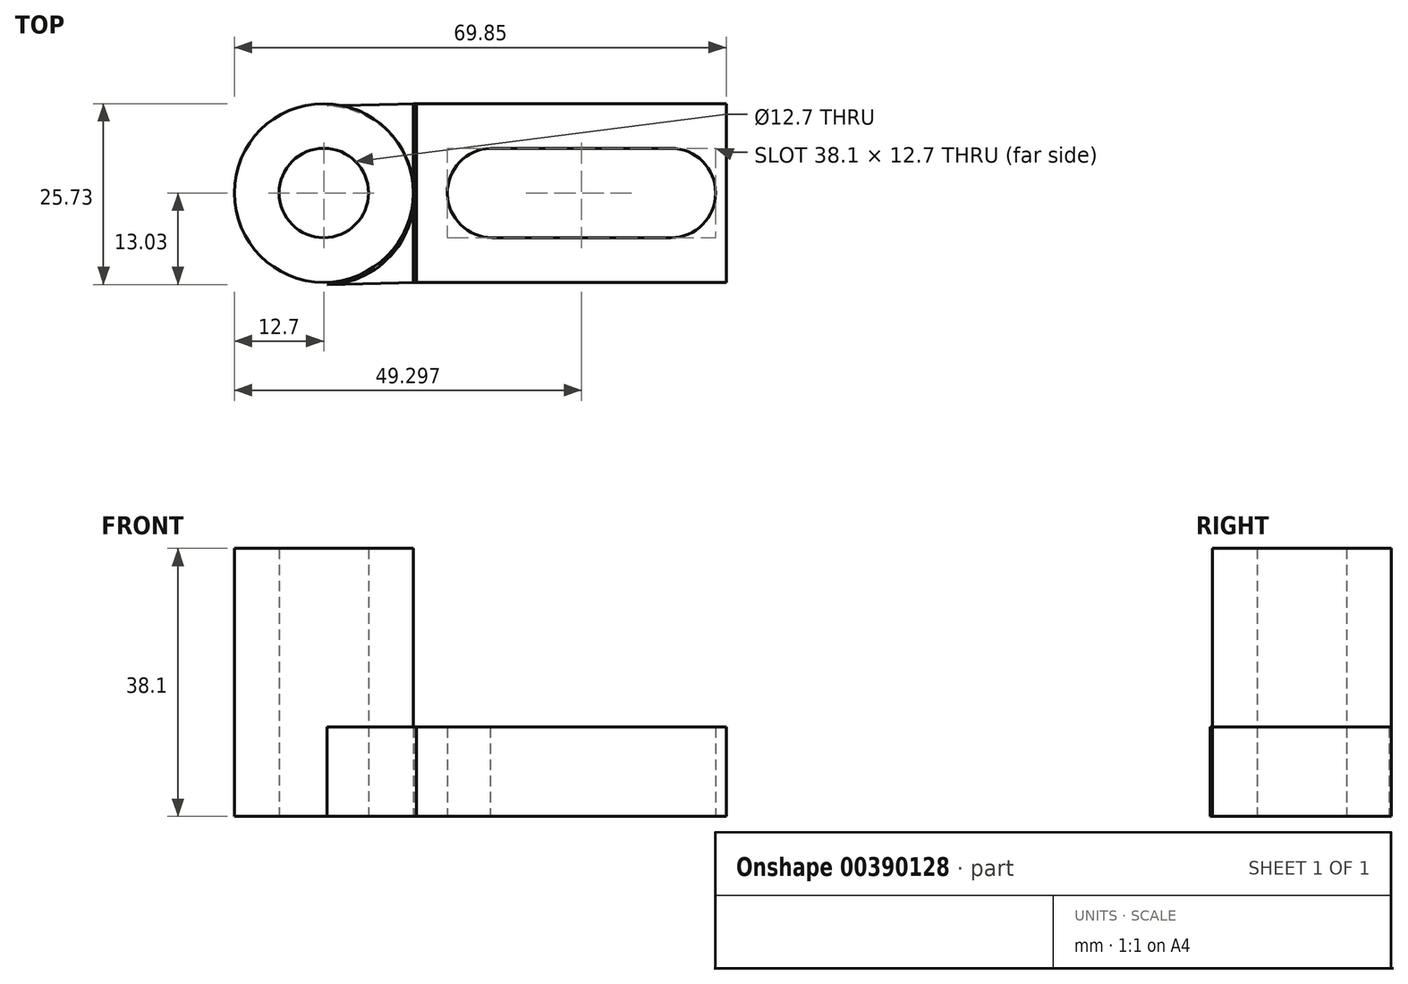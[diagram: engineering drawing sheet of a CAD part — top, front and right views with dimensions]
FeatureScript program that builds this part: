
annotation { "Feature Type Name" : "Feature", "Feature Type Description" : "" }
export const myFeature = defineFeature(function(context is Context, id is Id, definition is map)
    precondition{}
    {
        {
            var Q0;
            Q0=qCreatedBy(makeId("Front.planeOp"),FACE);
            var sketch = newSketch(context, id + "F0", { "sketchPlane" : qUnion([Q0])});
            skLineSegment(sketch, "E0", {"start": v(0, 0) * mm, "end": v(69.85, 0) * mm});
            skLineSegment(sketch, "E1", {"start": v(69.85, 0) * mm, "end": v(69.85, 12.7) * mm});
            skLineSegment(sketch, "E2", {"start": v(69.85, 12.7) * mm, "end": v(25.4, 12.7) * mm});
            skLineSegment(sketch, "E3", {"start": v(25.4, 12.7) * mm, "end": v(25.4, 38.1) * mm});
            skLineSegment(sketch, "E4", {"start": v(25.4, 38.1) * mm, "end": v(0, 38.1) * mm});
            skLineSegment(sketch, "E5", {"start": v(0, 38.1) * mm, "end": v(0, 0) * mm});
            skSolve(sketch);
        }
        {
            var Q0;
            Q0=makeQuery(id+"F0.imprint","IMPRINT",FACE,{"disambiguationData":[TD([[makeQuery(id+"F0.imprint","IMPRINT",EDGE,{"derivedFrom":sQuery(id+"F0.wireOp",EDGE,"E0")}),1.0]])]});
            extrude(context, id + "F1", {"entities" : qUnion([Q0]), "depth" : 25.4 * mm});
        }
        {
            var Q0;
            Q0=qCreatedBy(makeId("Top.planeOp"),FACE);
            var sketch = newSketch(context, id + "F2", { "sketchPlane" : qUnion([Q0])});
            skCircle(sketch, "E6", {"center": v(36.6, -12.7) * mm, "radius": 6.35 * mm});
            skCircle(sketch, "E7", {"center": v(62, -12.7) * mm, "radius": 6.35 * mm});
            skLineSegment(sketch, "E8", {"start": v(36.35, -6.35) * mm, "end": v(62, -6.35) * mm});
            skLineSegment(sketch, "E9", {"start": v(62, -6.35) * mm, "end": v(62, -19.05) * mm});
            skLineSegment(sketch, "E10", {"start": v(62, -19.05) * mm, "end": v(36.6, -19.05) * mm});
            skLineSegment(sketch, "E11", {"start": v(36.6, -19.05) * mm, "end": v(36.35, -6.35) * mm});
            skLineSegment(sketch, "E12", {"start": v(0, 0) * mm, "end": v(0, -25.4) * mm});
            skLineSegment(sketch, "E13", {"start": v(0, -25.4) * mm, "end": v(25.4, -25.4) * mm});
            skLineSegment(sketch, "E14", {"start": v(25.4, -25.4) * mm, "end": v(25.4, 0) * mm});
            skLineSegment(sketch, "E15", {"start": v(25.4, 0) * mm, "end": v(0, 0) * mm});
            skSolve(sketch);
        }
        {
            var Q0;
            {var subQ0=sQuery(id+"F2.wireOp",EDGE,"E10");Q0=makeQuery(id+"F2.imprint","IMPRINT",FACE,{"disambiguationData":[TD([[makeQuery(id+"F2.imprint","IMPRINT",EDGE,{"derivedFrom":subQ0}),-1.0]])]});}
            var Q1;
            {var subQ0=sQuery(id+"F2.wireOp",EDGE,"E9");Q1=makeQuery(id+"F2.imprint","IMPRINT",FACE,{"disambiguationData":[TD([[makeQuery(id+"F2.imprint","IMPRINT",EDGE,{"derivedFrom":subQ0}),-1.0]])]});}
            var Q2;
            {var subQ0=sQuery(id+"F2.wireOp",EDGE,"E9");Q2=makeQuery(id+"F2.imprint","IMPRINT",FACE,{"disambiguationData":[TD([[makeQuery(id+"F2.imprint","IMPRINT",EDGE,{"derivedFrom":subQ0}),1.0]])]});}
            var Q3;
            {var subQ0=sQuery(id+"F2.wireOp",EDGE,"E11");Q3=makeQuery(id+"F2.imprint","IMPRINT",FACE,{"disambiguationData":[TD([[makeQuery(id+"F2.imprint","IMPRINT",EDGE,{"derivedFrom":subQ0}),-1.0]])]});}
            var Q4;
            {var subQ0=sQuery(id+"F2.wireOp",EDGE,"E11");Q4=makeQuery(id+"F2.imprint","IMPRINT",FACE,{"disambiguationData":[TD([[makeQuery(id+"F2.imprint","IMPRINT",EDGE,{"derivedFrom":subQ0}),1.0]])]});}
            extrude(context, id + "F3", {"entities" : qUnion([Q0, Q1, Q2, Q3, Q4]), "operationType" : NewBodyOperationType.REMOVE, "depth" : 50.8 * mm});
        }
        {
            var Q0;
            Q0=qCreatedBy(makeId("Top.planeOp"),FACE);
            var sketch = newSketch(context, id + "F4", { "sketchPlane" : qUnion([Q0])});
            skCircle(sketch, "E16", {"center": v(12.7, -12.7) * mm, "radius": 6.35 * mm});
            skArc(sketch, "E17", {"start": v(12.7, -25.4) * mm, "mid": v(0, -12.7) * mm, "end": v(12.7, 0) * mm});
            skLineSegment(sketch, "E18", {"start": v(12.7, 0) * mm, "end": v(0, 0) * mm});
            skLineSegment(sketch, "E19", {"start": v(0, 0) * mm, "end": v(0, -25.4) * mm});
            skLineSegment(sketch, "E20", {"start": v(0, -25.4) * mm, "end": v(12.7, -25.4) * mm});
            skArc(sketch, "E21", {"start": v(12.7, 0) * mm, "mid": v(25.4, -12.7) * mm, "end": v(12.7, -25.4) * mm});
            skLineSegment(sketch, "E22", {"start": v(12.7, -25.4) * mm, "end": v(25.4, -25.4) * mm});
            skLineSegment(sketch, "E23", {"start": v(25.4, -25.4) * mm, "end": v(25.4, 0) * mm});
            skLineSegment(sketch, "E24", {"start": v(25.4, 0) * mm, "end": v(12.7, 0) * mm});
            skSolve(sketch);
        }
        {
            var Q0;
            {var subQ0=sQuery(id+"F4.wireOp",EDGE,"E20");Q0=makeQuery(id+"F4.imprint","IMPRINT",FACE,{"disambiguationData":[TD([[makeQuery(id+"F4.imprint","IMPRINT",EDGE,{"derivedFrom":subQ0}),1.0]])]});}
            var Q1;
            {var subQ0=sQuery(id+"F4.wireOp",EDGE,"E18");Q1=makeQuery(id+"F4.imprint","IMPRINT",FACE,{"disambiguationData":[TD([[makeQuery(id+"F4.imprint","IMPRINT",EDGE,{"derivedFrom":subQ0}),1.0]])]});}
            var Q2;
            {var subQ0=sQuery(id+"F4.wireOp",EDGE,"E24");Q2=makeQuery(id+"F4.imprint","IMPRINT",FACE,{"disambiguationData":[TD([[makeQuery(id+"F4.imprint","IMPRINT",EDGE,{"derivedFrom":subQ0}),1.0]])]});}
            var Q3;
            {var subQ0=sQuery(id+"F4.wireOp",EDGE,"E22");Q3=makeQuery(id+"F4.imprint","IMPRINT",FACE,{"disambiguationData":[TD([[makeQuery(id+"F4.imprint","IMPRINT",EDGE,{"derivedFrom":subQ0}),1.0]])]});}
            var Q4;
            Q4=makeQuery(id+"F4.imprint","IMPRINT",FACE,{"disambiguationData":[TD([[makeQuery(id+"F4.imprint","IMPRINT",EDGE,{"derivedFrom":sQuery(id+"F4.wireOp",EDGE,"E16")}),1.0]])]});
            extrude(context, id + "F5", {"entities" : qUnion([Q0, Q1, Q2, Q3, Q4]), "operationType" : NewBodyOperationType.REMOVE, "depth" : 50.8 * mm});
        }
        {
            var Q0;
            Q0=qCreatedBy(makeId("Top.planeOp"),FACE);
            var sketch = newSketch(context, id + "F6", { "sketchPlane" : qUnion([Q0])});
            skArc(sketch, "E25", {"start": v(13.18, -25.73) * mm, "mid": v(25.55, -13.03) * mm, "end": v(13.18, -0.33) * mm});
            skLineSegment(sketch, "E26", {"start": v(13.18, -25.73) * mm, "end": v(25.88, -25.4) * mm});
            skLineSegment(sketch, "E27", {"start": v(25.88, -25.4) * mm, "end": v(25.88, 0) * mm});
            skLineSegment(sketch, "E28", {"start": v(25.88, 0) * mm, "end": v(13.18, -0.33) * mm});
            skSolve(sketch);
        }
        {
            var Q0;
            {var subQ0=sQuery(id+"F6.wireOp",EDGE,"RLF4N8kG-6ZYG-Erl5-EgZC-uOB70CUtHSlL");Q0=makeQuery(id+"F6.imprint","IMPRINT",FACE,{"disambiguationData":[TD([[makeQuery(id+"F6.imprint","IMPRINT",EDGE,{"derivedFrom":subQ0}),-1.0]])]});}
            var Q1;
            {var subQ0=sQuery(id+"F6.wireOp",EDGE,"vE5mpCiB-Dx1T-hQNO-CaQA-q3kFRW5skTAE");Q1=makeQuery(id+"F6.imprint","IMPRINT",FACE,{"disambiguationData":[TD([[makeQuery(id+"F6.imprint","IMPRINT",EDGE,{"derivedFrom":subQ0}),-1.0]])]});}
            var Q2;
            Q2=makeQuery(id+"F6.imprint","IMPRINT",FACE,{"disambiguationData":[TD([[makeQuery(id+"F6.imprint","IMPRINT",EDGE,{"derivedFrom":sQuery(id+"F6.wireOp",EDGE,"E25")}),-1.0]])]});
            extrude(context, id + "F7", {"entities" : qUnion([Q0, Q1, Q2]), "depth" : 12.7 * mm});
        }
    });
